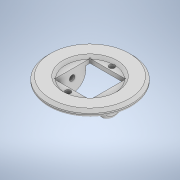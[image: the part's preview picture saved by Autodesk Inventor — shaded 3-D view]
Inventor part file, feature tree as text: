
AUTODESK INVENTOR PART (.ipt)
format: ipt  version: 2022 (Build 260153000, 153)  size: 211,456 bytes
history: native  units: in
note: dims shown in document units (in); Inventor stores cm internally (conversion verified against a paired STEP export)
features: extrude x6, sketch x6, chamfer x2, fillet x2
ambient origin geometry x8: Origin, YZ Plane, XZ Plane, XY Plane, X Axis, Y Axis, Z Axis, Center Point
bodies: Solid1 (feature_tree)
feature tree (16):
  extrude  "Extrusion1"  Depth=0.1969in TaperAngle=0.0deg
  extrude  "Extrusion2"  Depth=0.0787in TaperAngle=0.0deg
  chamfer  "Chamfer1"  Distance=0.0787in Angle=45.0deg
  extrude  "Extrusion3"  Depth=1.0394in
  extrude  "Extrusion4"  Depth=0.1575in
  extrude  "Extrusion5"  Depth=0.7874in TaperAngle=0.0deg
  fillet  "Fillet1"  Radius=0.1969in
  fillet  "Fillet2"  Radius=0.7874in
  extrude  "Extrusion6"  Depth=0.7874in
  chamfer  "Chamfer2"  Distance=0.5079in
  sketch  "Sketch1"  dims[d0=2.4409in d1=0.1969in d2=0.0in]
  sketch  "Sketch2"  dims[d3=1.5748in d4=0.0787in d5=0.0in d6=0.0787in d7=0.0787in d8=45.0deg]
  sketch  "Sketch3"  dims[d9=1.0394in d10=1.0394in]
  sketch  "Sketch4"  dims[d11=0.2362in d12=0.0in d13=0.1575in]
  sketch  "Sketch5"  dims[d14=0.1575in d15=0.2362in d16=0.0in d17=0.1969in d18=0.7874in]
  sketch  "Sketch6"  dims[d19=0.1969in d20=0.7874in d21=0.5079in d22=0.0in d23=0.3937in d24=0.0787in d25=0.1575in d26=1.9685in d27=0.0in d28=0.0787in d29=0.0787in d30=45.0deg d31=0.0197in d32=0.0344in d33=0.0197in d34=0.0344in]
